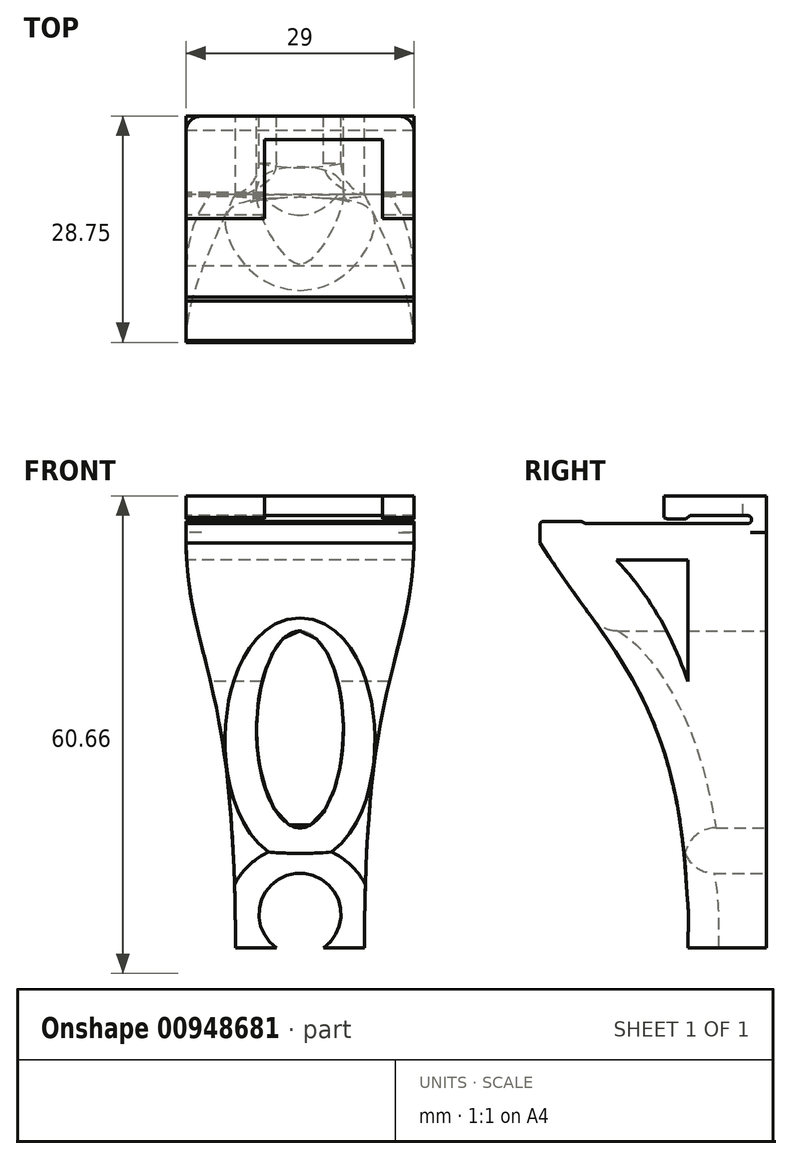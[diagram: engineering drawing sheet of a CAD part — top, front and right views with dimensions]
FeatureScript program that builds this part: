
annotation { "Feature Type Name" : "Feature", "Feature Type Description" : "" }
export const myFeature = defineFeature(function(context is Context, id is Id, definition is map)
    precondition{}
    {
        {
            var Q0;
            Q0=qCreatedBy(makeId("Top.planeOp"),FACE);
            var sketch = newSketch(context, id + "F0", { "sketchPlane" : qUnion([Q0])});
            skLineSegment(sketch, "E0", {"start": v(7.5, 0) * mm, "end": v(11.5, 0) * mm});
            skLineSegment(sketch, "E1", {"start": v(-7.5, 0) * mm, "end": v(-17.5, 0) * mm});
            skLineSegment(sketch, "E2", {"start": v(-17.5, 0) * mm, "end": v(-17.5, 10) * mm});
            skLineSegment(sketch, "E3", {"start": v(11.5, 10) * mm, "end": v(11.5, 0) * mm});
            skLineSegment(sketch, "E4", {"start": v(7.5, 0) * mm, "end": v(7.5, 10) * mm});
            skLineSegment(sketch, "E5", {"start": v(-7.5, 0) * mm, "end": v(-7.5, 10) * mm});
            skLineSegment(sketch, "E6.top", {"start": v(11.5, 13) * mm, "end": v(-17.5, 13) * mm});
            skLineSegment(sketch, "E6.left", {"start": v(11.5, 10) * mm, "end": v(11.5, 13) * mm});
            skLineSegment(sketch, "E6.right", {"start": v(-17.5, 10) * mm, "end": v(-17.5, 13) * mm});
            skLineSegment(sketch, "E7", {"start": v(7.5, 10) * mm, "end": v(-7.5, 10) * mm});
            skSolve(sketch);
        }
        {
            var Q0;
            Q0=makeQuery(id+"F0.imprint","IMPRINT",FACE,{"disambiguationData":[TD([[makeQuery(id+"F0.imprint","IMPRINT",EDGE,{"derivedFrom":sQuery(id+"F0.wireOp",EDGE,"E0")}),1.0]])]});
            var Q1;
            Q1=makeQuery(id+"F0.imprint","IMPRINT",FACE,{"disambiguationData":[TD([[makeQuery(id+"F0.imprint","IMPRINT",EDGE,{"derivedFrom":sQuery(id+"F0.wireOp",EDGE,"E6.top")}),1.0]])]});
            var Q2;
            Q2=makeQuery(id+"F0.imprint","IMPRINT",FACE,{"disambiguationData":[TD([[makeQuery(id+"F0.imprint","IMPRINT",EDGE,{"derivedFrom":sQuery(id+"F0.wireOp",EDGE,"E1")}),-1.0]])]});
            extrude(context, id + "F1", {"entities" : qUnion([Q0, Q1, Q2]), "oppositeDirection" : true, "depth" : 6 * mm, "offsetDistance" : 25 * mm});
        }
        {
            var Q0;
            Q0=sQuery(id+"F0.wireOp",EDGE,"E2");
            cPlane(context, id + "F2", {"entities" : qUnion([Q0]), "cplaneType" : CPlaneType.LINE_ANGLE, "offset" : 25 * mm, "angle" : 270 * degree, "width" : 150 * mm, "height" : 150 * mm});
        }
        {
            var Q0;
            Q0=qCreatedBy(id+"F2.planeOp",FACE);
            var sketch = newSketch(context, id + "F3", { "sketchPlane" : qUnion([Q0])});
            skLineSegment(sketch, "E8", {"start": v(-13.09, 0) * mm, "end": v(0, -6) * mm, "construction": true});
            skLineSegment(sketch, "E9", {"start": v(0, 0) * mm, "end": v(-13, -6) * mm, "construction": true});
            skPoint(sketch, "E10", {"position": v(-6.53, -3.01) * mm});
            skLineSegment(sketch, "E11", {"start": v(-11.13, -3.51) * mm, "end": v(-3.26, -3.51) * mm});
            skLineSegment(sketch, "E12", {"start": v(-11.13, -3.51) * mm, "end": v(-11.13, -2.51) * mm});
            skLineSegment(sketch, "E13.MirrorCS", {"start": v(-11.13, -2.51) * mm, "end": v(-3.26, -2.51) * mm});
            skLineSegment(sketch, "E14", {"start": v(-6.53, -3.01) * mm, "end": v(-9.57, -3.01) * mm, "construction": true});
            skLineSegment(sketch, "E15.MirrorCS", {"start": v(-3.26, -2.51) * mm, "end": v(-2.75, -2.96) * mm});
            skLineSegment(sketch, "E16.MirrorCS", {"start": v(-2.75, -2.96) * mm, "end": v(-0.42, -2.96) * mm});
            skLineSegment(sketch, "E17.MirrorCS", {"start": v(-0.42, -2.96) * mm, "end": v(0, -2.77) * mm});
            skLineSegment(sketch, "E18", {"start": v(-0.7, -3.51) * mm, "end": v(10, -3.51) * mm});
            skLineSegment(sketch, "E19", {"start": v(10, -3.51) * mm, "end": v(10.5, -3.26) * mm});
            skLineSegment(sketch, "E20", {"start": v(10.5, -3.26) * mm, "end": v(15.5, -3.26) * mm});
            skLineSegment(sketch, "E21", {"start": v(15.5, -3.26) * mm, "end": v(15.75, -3.51) * mm});
            skLineSegment(sketch, "E22", {"start": v(15.75, -3.51) * mm, "end": v(15.75, -6) * mm});
            skLineSegment(sketch, "E23", {"start": v(-3.26, -3.51) * mm, "end": v(0, -3.51) * mm});
            skLineSegment(sketch, "E24", {"start": v(0, -2.77) * mm, "end": v(0, -3.51) * mm});
            skLineSegment(sketch, "E25", {"start": v(-13, -4.67) * mm, "end": v(-13, -56) * mm});
            skLineSegment(sketch, "E26", {"start": v(-13, -56) * mm, "end": v(-3, -56) * mm});
            skFitSpline(sketch, "E27", {"points": [v(-3, -56) * mm, v(15.75, -6) * mm], "startDerivative": vector(-0.06, 88.39) * mm, "endDerivative": vector(27.7, 43.66) * mm});
            skLineSegment(sketch, "E28", {"start": v(-3, -8.16) * mm, "end": v(6.06, -8.16) * mm});
            skLineSegment(sketch, "E29", {"start": v(-3, -8.16) * mm, "end": v(-3, -23.59) * mm});
            skFitSpline(sketch, "E30", {"points": [v(-3, -23.59) * mm, v(6.06, -8.16) * mm], "startDerivative": vector(5.62, 17.25) * mm, "endDerivative": vector(12.7, 13.39) * mm});
            skLineSegment(sketch, "E31", {"start": v(-13, -4.67) * mm, "end": v(-0.7, -4.67) * mm});
            skLineSegment(sketch, "E32", {"start": v(-0.7, -4.67) * mm, "end": v(-0.7, -3.51) * mm});
            skSolve(sketch);
        }
        {
            var Q0;
            Q0=makeQuery(id+"F3.imprint","IMPRINT",FACE,{"disambiguationData":[TD([[makeQuery(id+"F3.imprint","IMPRINT",EDGE,{"derivedFrom":sQuery(id+"F3.wireOp",EDGE,"E11")}),1.0]])]});
            extrude(context, id + "F4", {"entities" : qUnion([Q0]), "operationType" : NewBodyOperationType.REMOVE, "oppositeDirection" : true, "depth" : 30 * mm, "offsetDistance" : 25 * mm});
        }
        {
            var Q0;
            Q0=makeQuery(id+"F4.boolean.opBoolean","COPY",EDGE,{"derivedFrom":makeQuery(id+"F4.opExtrude","SWEPT_EDGE",EDGE,{"disambiguationData":[OSD([sQuery(id+"F3.wireOp",EDGE,"E11"),sQuery(id+"F3.wireOp",EDGE,"E12")])]})});
            var Q1;
            Q1=makeQuery(id+"F4.boolean.opBoolean","COPY",EDGE,{"derivedFrom":makeQuery(id+"F4.opExtrude","SWEPT_EDGE",EDGE,{"disambiguationData":[OSD([sQuery(id+"F3.wireOp",EDGE,"E12"),sQuery(id+"F3.wireOp",EDGE,"E13.MirrorCS")])]})});
            fillet(context, id + "F5", {"entities" : qUnion([Q0, Q1]), "radius" : .5 * mm, "tangentPropagation" : true, "allowEdgeOverflow" : false});
        }
        {
            var Q0;
            Q0=makeQuery(id+"F3.imprint","IMPRINT",FACE,{"disambiguationData":[TD([[makeQuery(id+"F3.imprint","IMPRINT",EDGE,{"derivedFrom":sQuery(id+"F3.wireOp",EDGE,"E18")}),-1.0]])]});
            extrude(context, id + "F6", {"entities" : qUnion([Q0]), "oppositeDirection" : true, "depth" : 29 * mm, "offsetDistance" : 25 * mm});
        }
        {
            var Q0;
            Q0=makeQuery(id+"F6.opExtrude","SWEPT_FACE",FACE,{"disambiguationData":[OSD([sQuery(id+"F3.wireOp",EDGE,"E25")])]});
            cPlane(context, id + "F7", {"entities" : qUnion([Q0]), "cplaneType" : CPlaneType.OFFSET, "offset" : 0 * mm, "width" : 150 * mm, "height" : 150 * mm});
        }
        {
            var Q0;
            Q0=qCreatedBy(id+"F7.planeOp",FACE);
            var sketch = newSketch(context, id + "F8", { "sketchPlane" : qUnion([Q0])});
            skLineSegment(sketch, "E33.bottom", {"start": v(17.5, -4.67) * mm, "end": v(-11.5, -4.67) * mm, "construction": true});
            skLineSegment(sketch, "E33.top", {"start": v(17.5, -54.67) * mm, "end": v(-11.5, -54.67) * mm, "construction": true});
            skLineSegment(sketch, "E33.left", {"start": v(17.5, -4.67) * mm, "end": v(17.5, -54.67) * mm, "construction": true});
            skLineSegment(sketch, "E33.right", {"start": v(-11.5, -4.67) * mm, "end": v(-11.5, -54.67) * mm, "construction": true});
            skPoint(sketch, "E34", {"position": v(17.5, -4.67) * mm});
            skLineSegment(sketch, "E35", {"start": v(-11.5, -4.67) * mm, "end": v(17.5, -54.67) * mm, "construction": true});
            skLineSegment(sketch, "E36", {"start": v(-11.5, -54.67) * mm, "end": v(17.5, -4.67) * mm, "construction": true});
            skPoint(sketch, "E37", {"position": v(3, -29.67) * mm});
            skLineSegment(sketch, "E38", {"start": v(3, -58.38) * mm, "end": v(3, -1.2) * mm, "construction": true});
            skLineSegment(sketch, "E39", {"start": v(-1.2, -57.4) * mm, "end": v(7.2, -57.4) * mm});
            skLineSegment(sketch, "E40", {"start": v(-1.2, -57.4) * mm, "end": v(-5.2, -57.4) * mm});
            skLineSegment(sketch, "E41", {"start": v(-5.2, -57.4) * mm, "end": v(-5.2, -0.79) * mm, "construction": true});
            skFitSpline(sketch, "E42", {"points": [v(-5.2, -57.4) * mm, v(-11.5, -4.67) * mm], "startDerivative": vector(0, 107.34) * mm, "endDerivative": vector(0, 48.14) * mm});
            skLineSegment(sketch, "E43", {"start": v(-5.2, -57.4) * mm, "end": v(-18.9, -57.4) * mm});
            skLineSegment(sketch, "E44", {"start": v(-18.9, -57.4) * mm, "end": v(-12.86, -4.67) * mm});
            skLineSegment(sketch, "E45", {"start": v(-12.86, -4.67) * mm, "end": v(-11.5, -4.67) * mm});
            skFitSpline(sketch, "E46.MirrorCS", {"points": [v(11.2, -57.4) * mm, v(17.5, -4.67) * mm], "startDerivative": vector(0, 107.34) * mm, "endDerivative": vector(0, 48.14) * mm});
            skLineSegment(sketch, "E47.MirrorCS", {"start": v(24.9, -57.4) * mm, "end": v(18.86, -4.67) * mm});
            skLineSegment(sketch, "E48.MirrorCS", {"start": v(11.2, -57.4) * mm, "end": v(24.9, -57.4) * mm});
            skLineSegment(sketch, "E49.MirrorCS", {"start": v(7.2, -57.4) * mm, "end": v(11.2, -57.4) * mm});
            skLineSegment(sketch, "E50.MirrorCS", {"start": v(18.86, -4.67) * mm, "end": v(17.5, -4.67) * mm});
            skLineSegment(sketch, "E51", {"start": v(-2, -54.67) * mm, "end": v(-5.2, -54.67) * mm});
            skLineSegment(sketch, "E52", {"start": v(-5.2, -54.67) * mm, "end": v(8, -54.67) * mm});
            skLineSegment(sketch, "E53", {"start": v(8, -54.67) * mm, "end": v(11.2, -54.67) * mm});
            skEllipse(sketch, "E54", {"center": v(3, -29.67) * mm, "majorRadius": 12.5 * mm, "minorRadius": 5.51 * mm, "majorAxis": v(0, 1)});
            skArc(sketch, "E55", {"start": v(0, -57.4) * mm, "mid": v(3, -47.93) * mm, "end": v(6, -57.4) * mm});
            skSolve(sketch);
        }
        {
            var Q0;
            {var subQ0=sQuery(id+"F8.wireOp",EDGE,"E43");Q0=makeQuery(id+"F8.imprint","IMPRINT",FACE,{"disambiguationData":[TD([[makeQuery(id+"F8.imprint","IMPRINT",EDGE,{"derivedFrom":subQ0}),-1.0]])]});}
            var Q1;
            Q1=makeQuery(id+"F8.imprint","IMPRINT",FACE,{"disambiguationData":[TD([[makeQuery(id+"F8.imprint","IMPRINT",EDGE,{"derivedFrom":sQuery(id+"F8.wireOp",EDGE,"E47.MirrorCS")}),1.0]])]});
            var Q2;
            Q2=makeQuery(id+"F8.imprint","IMPRINT",FACE,{"disambiguationData":[TD([[makeQuery(id+"F8.imprint","IMPRINT",EDGE,{"derivedFrom":sQuery(id+"F8.wireOp",EDGE,"E54")}),1.0]])]});
            var Q3;
            {var subQ0=sQuery(id+"F8.wireOp",EDGE,"E55");var subQ1=sQuery(id+"F8.wireOp",EDGE,"E52");var subQ2=makeQuery(id+"F8.imprint","INTERSECT",VERTEX,{"disambiguationData":[OD(0.0)],"derivedFrom":[subQ1,subQ0]});Q3=makeQuery(id+"F8.imprint","IMPRINT",FACE,{"disambiguationData":[TD([[makeQuery(id+"F8.imprint","IMPRINT",EDGE,{"disambiguationData":[TD([[subQ2,-1.0]])],"derivedFrom":subQ1}),1.0]])]});}
            var Q4;
            {var subQ0=sQuery(id+"F8.wireOp",EDGE,"E55");var subQ1=sQuery(id+"F8.wireOp",EDGE,"E39");var subQ2=makeQuery(id+"F8.imprint","INTERSECT",VERTEX,{"disambiguationData":[OD(0.0)],"derivedFrom":[subQ1,subQ0]});Q4=makeQuery(id+"F8.imprint","IMPRINT",FACE,{"disambiguationData":[TD([[makeQuery(id+"F8.imprint","IMPRINT",EDGE,{"disambiguationData":[TD([[subQ2,-1.0]])],"derivedFrom":subQ1}),1.0]])]});}
            extrude(context, id + "F9", {"entities" : qUnion([Q0, Q1, Q2, Q3, Q4]), "operationType" : NewBodyOperationType.REMOVE, "oppositeDirection" : true, "depth" : 30 * mm, "offsetDistance" : 25 * mm});
        }
        {
            var Q0;
            {var subQ0=sQuery(id+"F8.wireOp",EDGE,"E40");Q0=makeQuery(id+"F8.imprint","IMPRINT",FACE,{"disambiguationData":[TD([[makeQuery(id+"F8.imprint","IMPRINT",EDGE,{"derivedFrom":subQ0}),-1.0]])]});}
            var Q1;
            {var subQ0=sQuery(id+"F8.wireOp",EDGE,"E49.MirrorCS");Q1=makeQuery(id+"F8.imprint","IMPRINT",FACE,{"disambiguationData":[TD([[makeQuery(id+"F8.imprint","IMPRINT",EDGE,{"derivedFrom":subQ0}),1.0]])]});}
            extrude(context, id + "F10", {"entities" : qUnion([Q0, Q1]), "operationType" : NewBodyOperationType.ADD, "oppositeDirection" : true, "depth" : 10 * mm, "offsetDistance" : 25 * mm});
        }
        {
            var Q0;
            Q0=makeQuery(id+"F9.boolean.opBoolean","COPY",EDGE,{"derivedFrom":makeQuery(id+"F9.opExtrude","CAP_EDGE",EDGE,{"disambiguationData":[OSD([sQuery(id+"F8.wireOp",EDGE,"E46.MirrorCS")])],"isStart":true})});
            var Q1;
            Q1=makeQuery(id+"F9.boolean.opBoolean","INTERSECT",EDGE,{"derivedFrom":[makeQuery(id+"F6.opExtrude","SWEPT_FACE",FACE,{"disambiguationData":[OSD([sQuery(id+"F3.wireOp",EDGE,"E27")])]}),makeQuery(id+"F9.opExtrude","SWEPT_FACE",FACE,{"disambiguationData":[OSD([sQuery(id+"F8.wireOp",EDGE,"E46.MirrorCS")])]})]});
            var Q2;
            Q2=makeQuery(id+"F9.boolean.opBoolean","INTERSECT",EDGE,{"derivedFrom":[makeQuery(id+"F6.opExtrude","SWEPT_FACE",FACE,{"disambiguationData":[OSD([sQuery(id+"F3.wireOp",EDGE,"E30")])]}),makeQuery(id+"F9.opExtrude","SWEPT_FACE",FACE,{"disambiguationData":[OSD([sQuery(id+"F8.wireOp",EDGE,"E46.MirrorCS")])]})]});
            var Q3;
            Q3=makeQuery(id+"F9.boolean.opBoolean","INTERSECT",EDGE,{"derivedFrom":[makeQuery(id+"F6.opExtrude","SWEPT_FACE",FACE,{"disambiguationData":[OSD([sQuery(id+"F3.wireOp",EDGE,"E28")])]}),makeQuery(id+"F9.opExtrude","SWEPT_FACE",FACE,{"disambiguationData":[OSD([sQuery(id+"F8.wireOp",EDGE,"E46.MirrorCS")])]})]});
            var Q4;
            Q4=makeQuery(id+"F9.boolean.opBoolean","INTERSECT",EDGE,{"derivedFrom":[makeQuery(id+"F6.opExtrude","SWEPT_FACE",FACE,{"disambiguationData":[OSD([sQuery(id+"F3.wireOp",EDGE,"E29")])]}),makeQuery(id+"F9.opExtrude","SWEPT_FACE",FACE,{"disambiguationData":[OSD([sQuery(id+"F8.wireOp",EDGE,"E46.MirrorCS")])]})]});
            var Q5;
            Q5=makeQuery(id+"F9.boolean.opBoolean","COPY",EDGE,{"derivedFrom":makeQuery(id+"F9.opExtrude","CAP_EDGE",EDGE,{"disambiguationData":[OSD([sQuery(id+"F8.wireOp",EDGE,"E42")])],"isStart":true})});
            var Q6;
            Q6=makeQuery(id+"F9.boolean.opBoolean","INTERSECT",EDGE,{"derivedFrom":[makeQuery(id+"F6.opExtrude","SWEPT_FACE",FACE,{"disambiguationData":[OSD([sQuery(id+"F3.wireOp",EDGE,"E27")])]}),makeQuery(id+"F9.opExtrude","SWEPT_FACE",FACE,{"disambiguationData":[OSD([sQuery(id+"F8.wireOp",EDGE,"E42")])]})]});
            var Q7;
            Q7=makeQuery(id+"F9.boolean.opBoolean","INTERSECT",EDGE,{"derivedFrom":[makeQuery(id+"F6.opExtrude","SWEPT_FACE",FACE,{"disambiguationData":[OSD([sQuery(id+"F3.wireOp",EDGE,"E30")])]}),makeQuery(id+"F9.opExtrude","SWEPT_FACE",FACE,{"disambiguationData":[OSD([sQuery(id+"F8.wireOp",EDGE,"E42")])]})]});
            var Q8;
            Q8=makeQuery(id+"F9.boolean.opBoolean","INTERSECT",EDGE,{"derivedFrom":[makeQuery(id+"F6.opExtrude","SWEPT_FACE",FACE,{"disambiguationData":[OSD([sQuery(id+"F3.wireOp",EDGE,"E28")])]}),makeQuery(id+"F9.opExtrude","SWEPT_FACE",FACE,{"disambiguationData":[OSD([sQuery(id+"F8.wireOp",EDGE,"E42")])]})]});
            var Q9;
            Q9=makeQuery(id+"F9.boolean.opBoolean","INTERSECT",EDGE,{"derivedFrom":[makeQuery(id+"F6.opExtrude","SWEPT_FACE",FACE,{"disambiguationData":[OSD([sQuery(id+"F3.wireOp",EDGE,"E29")])]}),makeQuery(id+"F9.opExtrude","SWEPT_FACE",FACE,{"disambiguationData":[OSD([sQuery(id+"F8.wireOp",EDGE,"E42")])]})]});
            var Q10;
            Q10=makeQuery(id+"F10.opExtrude","SWEPT_EDGE",EDGE,{"disambiguationData":[OSD([sQuery(id+"F8.wireOp",EDGE,"E46.MirrorCS"),sQuery(id+"F8.wireOp",EDGE,"E48.MirrorCS"),sQuery(id+"F8.wireOp",EDGE,"E49.MirrorCS")])]});
            var Q11;
            Q11=makeQuery(id+"F10.opExtrude","SWEPT_EDGE",EDGE,{"disambiguationData":[OSD([sQuery(id+"F8.wireOp",EDGE,"E40"),sQuery(id+"F8.wireOp",EDGE,"E42"),sQuery(id+"F8.wireOp",EDGE,"E43")])]});
            var Q12;
            Q12=makeQuery(id+"F1.opExtrude","SWEPT_EDGE",EDGE,{"disambiguationData":[OSD([sQuery(id+"F0.wireOp",EDGE,"E6.top"),sQuery(id+"F0.wireOp",EDGE,"E6.right")])]});
            var Q13;
            Q13=makeQuery(id+"F1.opExtrude","SWEPT_EDGE",EDGE,{"disambiguationData":[OSD([sQuery(id+"F0.wireOp",EDGE,"E6.top"),sQuery(id+"F0.wireOp",EDGE,"E6.left")])]});
            fillet(context, id + "F11", {"entities" : qUnion([Q0, Q1, Q2, Q3, Q4, Q5, Q6, Q7, Q8, Q9, Q10, Q11, Q12, Q13]), "radius" : 2 * mm, "tangentPropagation" : true, "allowEdgeOverflow" : false});
        }
        {
            var Q0;
            Q0=makeQuery(id+"F6.opExtrude","SWEPT_FACE",FACE,{"disambiguationData":[OSD([sQuery(id+"F3.wireOp",EDGE,"E18"),sQuery(id+"F3.wireOp",EDGE,"E23")])]});
            cPlane(context, id + "F12", {"entities" : qUnion([Q0]), "cplaneType" : CPlaneType.OFFSET, "offset" : 0 * mm, "width" : 150 * mm, "height" : 150 * mm});
        }
        {
            var Q0;
            Q0=qCreatedBy(id+"F12.planeOp",FACE);
            var sketch = newSketch(context, id + "F13", { "sketchPlane" : qUnion([Q0])});
            skLineSegment(sketch, "E56", {"start": v(0, 0) * mm, "end": v(-8.17, 0) * mm});
            skLineSegment(sketch, "E57", {"start": v(-8.17, 0) * mm, "end": v(-8.17, 10.95) * mm});
            skLineSegment(sketch, "E58", {"start": v(-8.17, 10.95) * mm, "end": v(8.78, 10.95) * mm});
            skLineSegment(sketch, "E59", {"start": v(8.78, 10.95) * mm, "end": v(8.78, 0) * mm});
            skLineSegment(sketch, "E60", {"start": v(8.78, 0) * mm, "end": v(0, 0) * mm});
            skSolve(sketch);
        }
        {
            var Q0;
            Q0=makeQuery(id+"F13.imprint","IMPRINT",FACE,{"disambiguationData":[TD([[makeQuery(id+"F13.imprint","IMPRINT",EDGE,{"derivedFrom":sQuery(id+"F13.wireOp",EDGE,"E56")}),-1.0]])]});
            extrude(context, id + "F14", {"entities" : qUnion([Q0]), "operationType" : NewBodyOperationType.ADD, "oppositeDirection" : true, "depth" : 2.5 * mm, "offsetDistance" : 25 * mm});
        }
        {
            var Q0;
            {var subQ0=sQuery(id+"F8.wireOp",EDGE,"E55");var subQ1=sQuery(id+"F8.wireOp",EDGE,"E39");Q0=makeQuery(id+"F10.boolean.opBoolean","MERGE",EDGE,{"derivedFrom":[makeQuery(id+"F9.boolean.opBoolean","COPY",EDGE,{"derivedFrom":makeQuery(id+"F9.opExtrude","CAP_EDGE",EDGE,{"disambiguationData":[OSD([subQ0])],"isStart":true})}),makeQuery(id+"F10.opExtrude","CAP_EDGE",EDGE,{"disambiguationData":[OSD([subQ0]),TDD([makeQuery(id+"F8.imprint","IMPRINT",EDGE,{"disambiguationData":[TD([[makeQuery(id+"F8.imprint","INTERSECT",VERTEX,{"disambiguationData":[OD(0.0)],"derivedFrom":[subQ1,subQ0]}),-1.0]])],"derivedFrom":subQ0})])],"isStart":true}),makeQuery(id+"F10.opExtrude","CAP_EDGE",EDGE,{"disambiguationData":[OSD([subQ0]),TDD([makeQuery(id+"F8.imprint","IMPRINT",EDGE,{"disambiguationData":[TD([[makeQuery(id+"F8.imprint","INTERSECT",VERTEX,{"disambiguationData":[OD(1.0)],"derivedFrom":[subQ1,subQ0]}),1.0]])],"derivedFrom":subQ0})])],"isStart":true})]});}
            var Q1;
            Q1=makeQuery(id+"F9.boolean.opBoolean","COPY",EDGE,{"derivedFrom":makeQuery(id+"F9.opExtrude","CAP_EDGE",EDGE,{"disambiguationData":[OSD([sQuery(id+"F8.wireOp",EDGE,"E54")])],"isStart":true})});
            var Q2;
            Q2=makeQuery(id+"F9.boolean.opBoolean","INTERSECT",EDGE,{"derivedFrom":[makeQuery(id+"F6.opExtrude","SWEPT_FACE",FACE,{"disambiguationData":[OSD([sQuery(id+"F3.wireOp",EDGE,"E27")])]}),makeQuery(id+"F9.opExtrude","SWEPT_FACE",FACE,{"disambiguationData":[OSD([sQuery(id+"F8.wireOp",EDGE,"E54")])]})]});
            var Q3;
            Q3=makeQuery(id+"F9.boolean.opBoolean","INTERSECT",EDGE,{"derivedFrom":[makeQuery(id+"F6.opExtrude","SWEPT_FACE",FACE,{"disambiguationData":[OSD([sQuery(id+"F3.wireOp",EDGE,"E27")])]}),makeQuery(id+"F9.opExtrude","SWEPT_FACE",FACE,{"disambiguationData":[OSD([sQuery(id+"F8.wireOp",EDGE,"E55")])]})]});
            fillet(context, id + "F15", {"entities" : qUnion([Q0, Q1, Q2, Q3]), "radius" : 4 * mm, "tangentPropagation" : true, "allowEdgeOverflow" : false});
        }
    });
